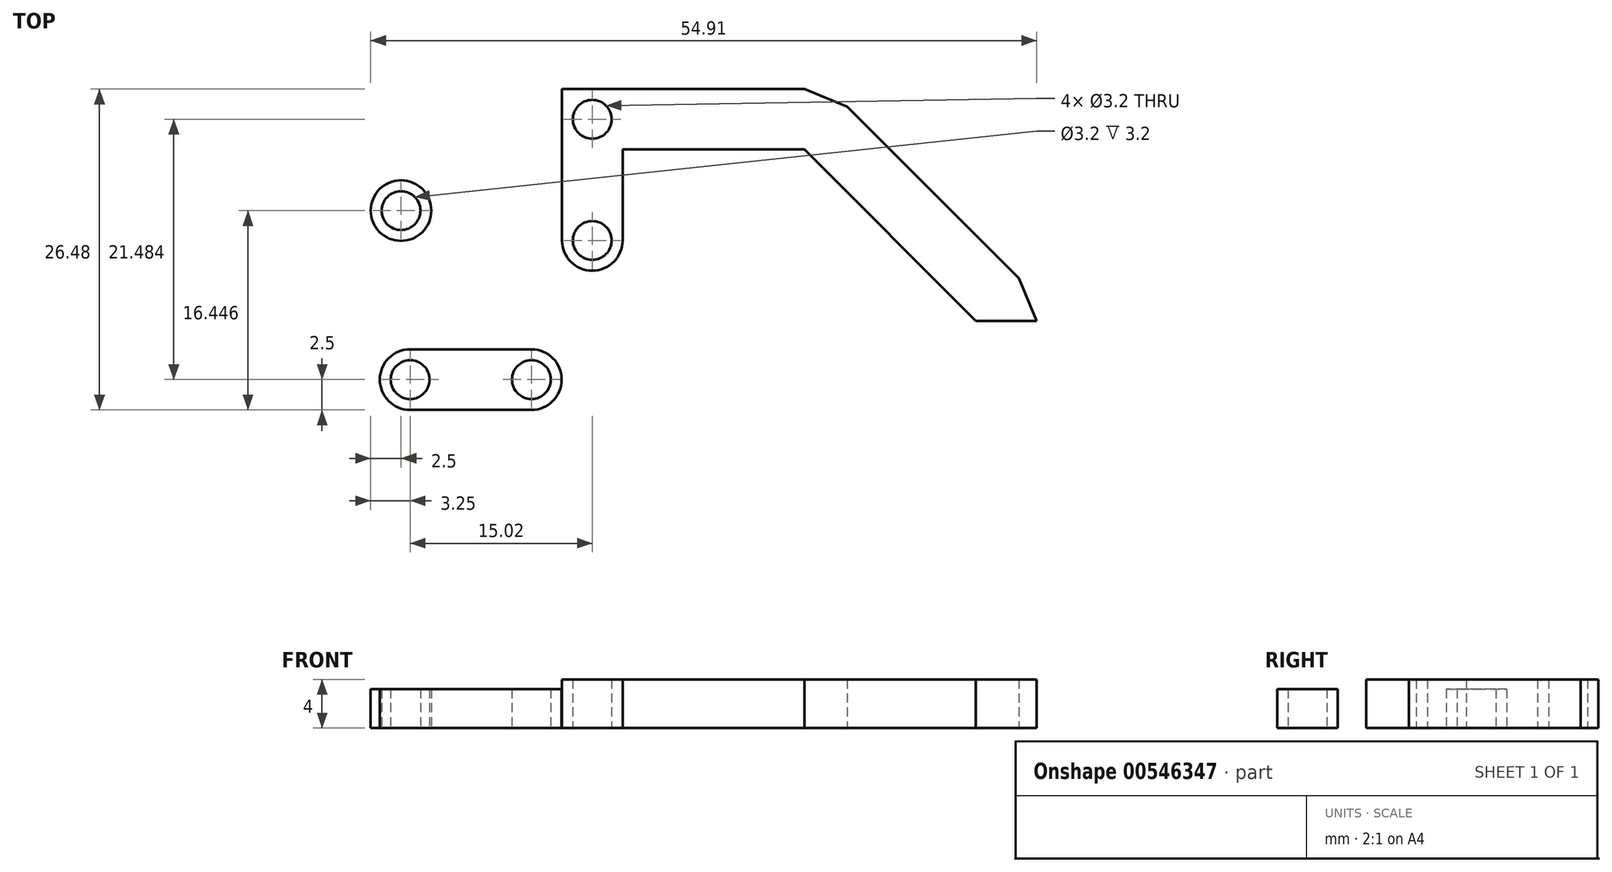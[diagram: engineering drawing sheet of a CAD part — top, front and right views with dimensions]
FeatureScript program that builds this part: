
annotation { "Feature Type Name" : "Feature", "Feature Type Description" : "" }
export const myFeature = defineFeature(function(context is Context, id is Id, definition is map)
    precondition{}
    {
        {
            var Q0;
            Q0=qCreatedBy(makeId("Top.planeOp"),FACE);
            var sketch = newSketch(context, id + "F0", { "sketchPlane" : qUnion([Q0])});
            skLineSegment(sketch, "E0", {"start": v(0, 21.48) * mm, "end": v(0, 16.48) * mm, "construction": true});
            skLineSegment(sketch, "E1", {"start": v(0, 16.48) * mm, "end": v(15, 16.48) * mm});
            skLineSegment(sketch, "E2", {"start": v(15, 16.48) * mm, "end": v(29.14, 2.34) * mm});
            skLineSegment(sketch, "E3", {"start": v(15, 16.48) * mm, "end": v(15, 21.48) * mm, "construction": true});
            skLineSegment(sketch, "E4", {"start": v(15, 21.48) * mm, "end": v(0, 21.48) * mm});
            skLineSegment(sketch, "E5", {"start": v(0, 16.48) * mm, "end": v(0, 8.98) * mm});
            skLineSegment(sketch, "E6", {"start": v(0, 8.98) * mm, "end": v(-5, 8.98) * mm, "construction": true});
            skLineSegment(sketch, "E7", {"start": v(-5, 8.98) * mm, "end": v(-5, 16.48) * mm});
            skLineSegment(sketch, "E8", {"start": v(-5, 16.48) * mm, "end": v(0, 16.48) * mm, "construction": true});
            skLineSegment(sketch, "E9", {"start": v(29.14, 2.34) * mm, "end": v(32.68, 5.88) * mm, "construction": true});
            skLineSegment(sketch, "E10", {"start": v(15, 16.48) * mm, "end": v(18.54, 20.02) * mm, "construction": true});
            skLineSegment(sketch, "E11", {"start": v(18.54, 20.02) * mm, "end": v(32.68, 5.88) * mm});
            skLineSegment(sketch, "E12", {"start": v(-2.5, 16.48) * mm, "end": v(-2.5, 18.98) * mm, "construction": true});
            skLineSegment(sketch, "E13", {"start": v(-2.5, 18.98) * mm, "end": v(0, 18.98) * mm, "construction": true});
            skCircle(sketch, "E14", {"center": v(-2.5, 18.98) * mm, "radius": 1.6 * mm});
            skLineSegment(sketch, "E15", {"start": v(-5, 16.48) * mm, "end": v(-5, 21.48) * mm});
            skLineSegment(sketch, "E16", {"start": v(-5, 21.48) * mm, "end": v(0, 21.48) * mm});
            skLineSegment(sketch, "E17", {"start": v(15, 21.48) * mm, "end": v(18.54, 20.02) * mm});
            skCircle(sketch, "E18", {"center": v(-2.5, 8.98) * mm, "radius": 2.5 * mm});
            skCircle(sketch, "E19", {"center": v(-2.5, 8.98) * mm, "radius": 1.6 * mm});
            skLineSegment(sketch, "E20", {"start": v(29.14, 2.34) * mm, "end": v(34.14, 2.34) * mm});
            skLineSegment(sketch, "E21", {"start": v(34.14, 2.34) * mm, "end": v(32.68, 5.88) * mm});
            skCircle(sketch, "E22", {"center": v(-7.52, -2.5) * mm, "radius": 2.5 * mm});
            skCircle(sketch, "E23", {"center": v(-7.52, -2.5) * mm, "radius": 1.6 * mm});
            skLineSegment(sketch, "E24", {"start": v(-7.52, 0) * mm, "end": v(-7.52, -5) * mm, "construction": true});
            skLineSegment(sketch, "E25", {"start": v(-7.52, -5) * mm, "end": v(-17.52, -5) * mm});
            skLineSegment(sketch, "E26", {"start": v(-17.52, -5) * mm, "end": v(-17.52, 0) * mm, "construction": true});
            skLineSegment(sketch, "E27", {"start": v(-17.52, 0) * mm, "end": v(-7.52, 0) * mm});
            skCircle(sketch, "E28", {"center": v(-17.52, -2.5) * mm, "radius": 2.5 * mm});
            skCircle(sketch, "E29", {"center": v(-17.52, -2.5) * mm, "radius": 1.6 * mm});
            skCircle(sketch, "E30", {"center": v(-18.27, 11.45) * mm, "radius": 2.5 * mm});
            skCircle(sketch, "E31", {"center": v(-18.27, 11.45) * mm, "radius": 1.6 * mm});
            skSolve(sketch);
        }
        {
            var Q0;
            Q0=makeQuery(id+"F0.imprint","IMPRINT",FACE,{"disambiguationData":[TD([[makeQuery(id+"F0.imprint","IMPRINT",EDGE,{"derivedFrom":sQuery(id+"F0.wireOp",EDGE,"E1")}),1.0]])]});
            var Q1;
            Q1=makeQuery(id+"F0.imprint","IMPRINT",FACE,{"disambiguationData":[TD([[makeQuery(id+"F0.imprint","IMPRINT",EDGE,{"derivedFrom":sQuery(id+"F0.wireOp",EDGE,"E19")}),-1.0]])]});
            extrude(context, id + "F1", {"entities" : qUnion([Q0, Q1]), "depth" : 4 * mm, "offsetDistance" : 25 * mm});
        }
        {
            var Q0;
            Q0=makeQuery(id+"F0.imprint","IMPRINT",FACE,{"disambiguationData":[TD([[makeQuery(id+"F0.imprint","IMPRINT",EDGE,{"derivedFrom":sQuery(id+"F0.wireOp",EDGE,"E23")}),-1.0]])]});
            var Q1;
            {var subQ0=sQuery(id+"F0.wireOp",EDGE,"E25");Q1=makeQuery(id+"F0.imprint","IMPRINT",FACE,{"disambiguationData":[TD([[makeQuery(id+"F0.imprint","IMPRINT",EDGE,{"derivedFrom":subQ0}),-1.0]])]});}
            var Q2;
            Q2=makeQuery(id+"F0.imprint","IMPRINT",FACE,{"disambiguationData":[TD([[makeQuery(id+"F0.imprint","IMPRINT",EDGE,{"derivedFrom":sQuery(id+"F0.wireOp",EDGE,"E29")}),-1.0]])]});
            extrude(context, id + "F2", {"entities" : qUnion([Q0, Q1, Q2]), "depth" : 3.2 * mm, "offsetDistance" : 25 * mm});
        }
        {
            var Q0;
            Q0=makeQuery(id+"F0.imprint","IMPRINT",FACE,{"disambiguationData":[TD([[makeQuery(id+"F0.imprint","IMPRINT",EDGE,{"derivedFrom":sQuery(id+"F0.wireOp",EDGE,"E30")}),1.0]])]});
            extrude(context, id + "F3", {"entities" : qUnion([Q0]), "depth" : 3.2 * mm, "offsetDistance" : 25 * mm});
        }
    });
